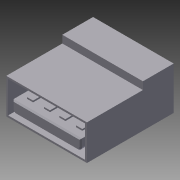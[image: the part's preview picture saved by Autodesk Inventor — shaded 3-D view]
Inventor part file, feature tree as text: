
AUTODESK INVENTOR PART (.ipt)
format: ipt  version: 2012 (Build 160160000, 160)  size: 153,088 bytes
history: native  units: mm
features: extrude x4, sketch x4, fillet x2, chamfer x2
ambient origin geometry x8: Origin, YZ Plane, XZ Plane, XY Plane, X Axis, Y Axis, Z Axis, Center Point
bodies: Solid1 (feature_tree)
feature tree (12):
  extrude  "Extrusion1"  Depth=14.1mm
  extrude  "Extrusion2"  Depth=5.0mm
  sketch  "Sketch3"  dims[d5=1.23mm d6=0.0mm d7=0.3mm d9=5.72mm d10=5.12mm]
  extrude  "Extrusion3"  Depth=0.3mm
  fillet  "Fillet3"  Radius=5.72mm
  fillet  "Fillet4"  Radius=5.12mm
  chamfer  "Chamfer1"  Distance=1.84mm
  chamfer  "Chamfer7"  Distance=0.7mm
  extrude  "Extrusion5"  Depth=10.3mm TaperAngle=0.0deg
  sketch  "Sketch1"  dims[d0=13.1mm d1=14.1mm]
  sketch  "Sketch2"  dims[d2=5.72mm d3=0.0mm d4=5.0mm]
  sketch  "Sketch4"  dims[d11=0.7mm d13=1.84mm d14=0.7mm d15=10.3mm d16=0.0mm d17=2.56mm d32=0.64mm d33=0.64mm d34=0.2mm d35=5.0mm d36=45.0deg d52=0.2mm d53=5.0mm d54=45.0deg d57=1.0mm d58=1.0mm d59=1.0mm d60=1.0mm d61=0.25mm d62=0.25mm d63=0.25mm d64=0.25mm d65=1.5mm d66=1.75mm d67=1.75mm d68=1.05mm d69=9.0mm d70=0.0mm]
